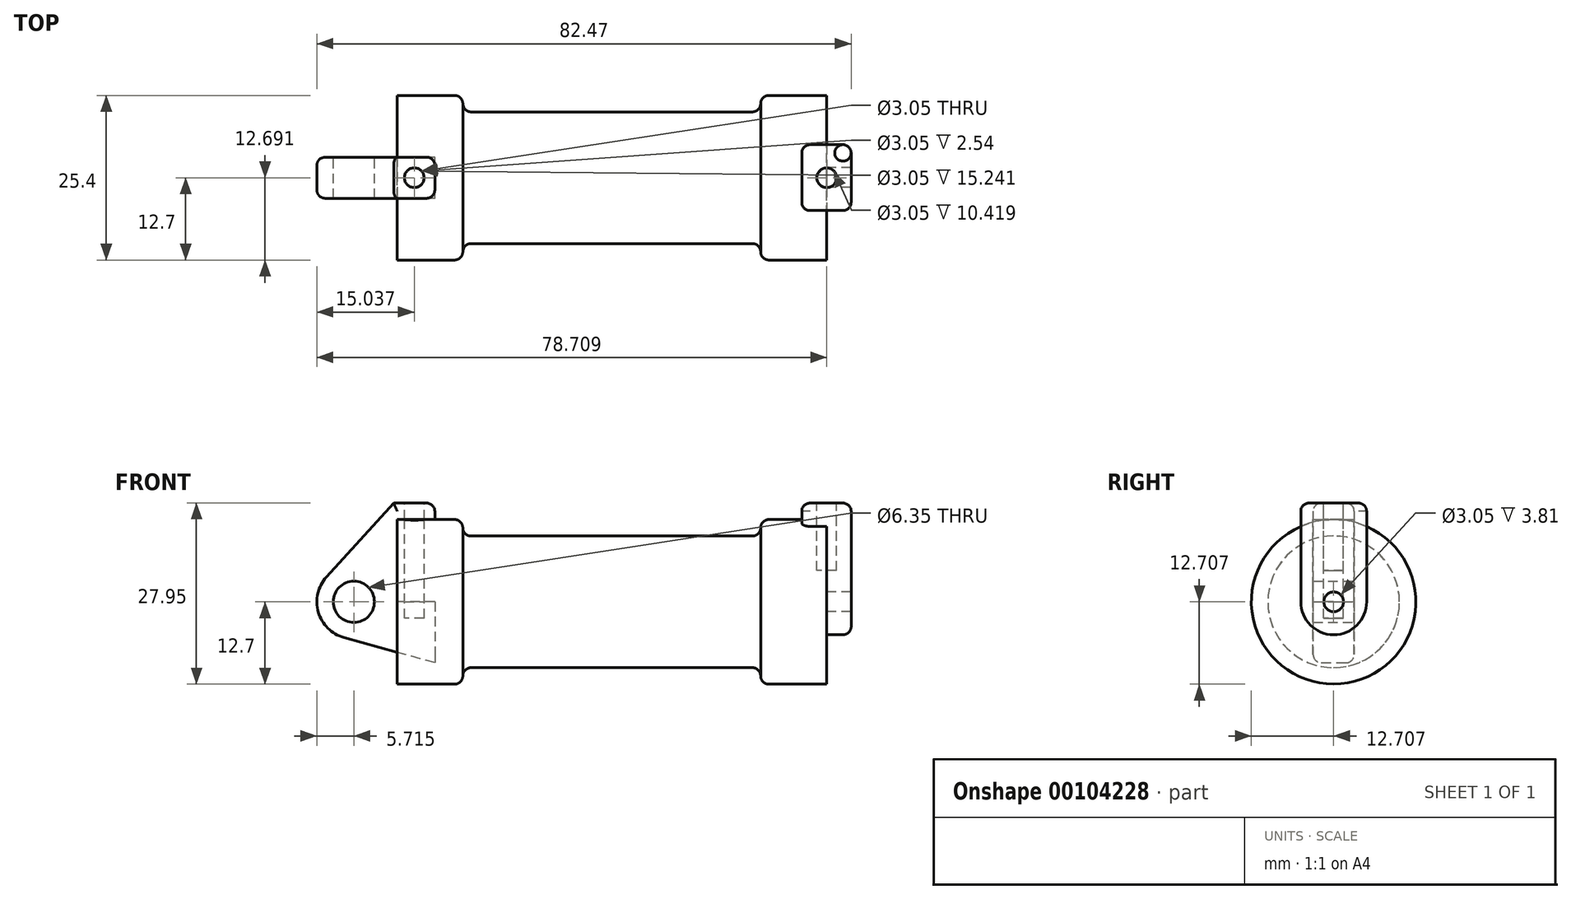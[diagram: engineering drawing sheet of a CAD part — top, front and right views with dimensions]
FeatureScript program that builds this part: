
annotation { "Feature Type Name" : "Feature", "Feature Type Description" : "" }
export const myFeature = defineFeature(function(context is Context, id is Id, definition is map)
    precondition{}
    {
        {
            var Q0;
            Q0=qCreatedBy(makeId("Front.planeOp"),FACE);
            var sketch = newSketch(context, id + "F0", { "sketchPlane" : qUnion([Q0])});
            skLineSegment(sketch, "E0", {"start": v(0, 0) * mm, "end": v(0, 12.7) * mm});
            skLineSegment(sketch, "E1", {"start": v(0, 12.7) * mm, "end": v(10.16, 12.7) * mm});
            skLineSegment(sketch, "E2", {"start": v(10.16, 12.7) * mm, "end": v(10.16, 10.16) * mm});
            skLineSegment(sketch, "E3", {"start": v(10.16, 10.16) * mm, "end": v(56.13, 10.16) * mm});
            skLineSegment(sketch, "E4", {"start": v(56.13, 10.16) * mm, "end": v(56.13, 12.7) * mm});
            skLineSegment(sketch, "E5", {"start": v(56.13, 12.7) * mm, "end": v(66.3, 12.7) * mm});
            skLineSegment(sketch, "E6", {"start": v(66.3, 12.7) * mm, "end": v(66.3, 0) * mm});
            skLineSegment(sketch, "E7", {"start": v(66.3, 0) * mm, "end": v(0, 0) * mm});
            skLineSegment(sketch, "E8", {"start": v(5.84, 15.24) * mm, "end": v(-0.5, 15.24) * mm});
            skLineSegment(sketch, "E9", {"start": v(-0.5, 15.24) * mm, "end": v(-10.88, 3.85) * mm});
            skLineSegment(sketch, "E10", {"start": v(0, 0) * mm, "end": v(-6.65, 0) * mm});
            skCircle(sketch, "E11", {"center": v(-6.65, 0) * mm, "radius": 5.72 * mm});
            skCircle(sketch, "E12", {"center": v(-6.65, 0) * mm, "radius": 3.18 * mm});
            skLineSegment(sketch, "E13", {"start": v(5.84, 15.24) * mm, "end": v(5.84, -9.4) * mm});
            skLineSegment(sketch, "E14", {"start": v(5.84, -9.4) * mm, "end": v(-8.18, -5.5) * mm});
            skSolve(sketch);
        }
        {
            var Q0;
            {var subQ0=sQuery(id+"F0.wireOp",EDGE,"E0");Q0=makeQuery(id+"F0.imprint","IMPRINT",FACE,{"disambiguationData":[TD([[makeQuery(id+"F0.imprint","IMPRINT",EDGE,{"derivedFrom":subQ0}),-1.0]])]});}
            var Q1;
            {var subQ0=sQuery(id+"F0.wireOp",EDGE,"E2");Q1=makeQuery(id+"F0.imprint","IMPRINT",FACE,{"disambiguationData":[TD([[makeQuery(id+"F0.imprint","IMPRINT",EDGE,{"derivedFrom":subQ0}),-1.0]])]});}
            var Q2;
            Q2=sQuery(id+"F0.wireOp",EDGE,"E7");
            revolve(context, id + "F1", {"entities" : qUnion([Q0, Q1]), "axis" : qUnion([Q2]), "revolveType" : RevolveType.FULL});
        }
        {
            var Q0;
            {var subQ4=sQuery(id+"F0.wireOp",EDGE,"E12");Q0=makeQuery(id+"F0.imprint","IMPRINT",FACE,{"disambiguationData":[TD([[makeQuery(id+"F0.imprint","IMPRINT",EDGE,{"derivedFrom":subQ4}),-1.0]])]});}
            var Q1;
            {var subQ3=sQuery(id+"F0.wireOp",EDGE,"E0");Q1=makeQuery(id+"F0.imprint","IMPRINT",FACE,{"disambiguationData":[TD([[makeQuery(id+"F0.imprint","IMPRINT",EDGE,{"derivedFrom":subQ3}),1.0]])]});}
            var Q2;
            {var subQ0=sQuery(id+"F0.wireOp",EDGE,"E14");Q2=makeQuery(id+"F0.imprint","IMPRINT",FACE,{"disambiguationData":[TD([[makeQuery(id+"F0.imprint","IMPRINT",EDGE,{"derivedFrom":subQ0}),-1.0]])]});}
            extrude(context, id + "F2", {"entities" : qUnion([Q0, Q1, Q2]), "endBound" : BoundingType.SYMMETRIC, "depth" : 6.35 * mm});
        }
        {
            var Q0;
            Q0=makeQuery(id+"F1.opRevolve","SWEPT_FACE",FACE,{"disambiguationData":[OSD([sQuery(id+"F0.wireOp",EDGE,"E6")])]});
            var sketch = newSketch(context, id + "F3", { "sketchPlane" : qUnion([Q0])});
            skPoint(sketch, "E15", {"position": v(0, 0) * mm});
            skCircle(sketch, "E16", {"center": v(0, 0) * mm, "radius": 1.52 * mm});
            skCircle(sketch, "E17", {"center": v(0, 0) * mm, "radius": 5.08 * mm});
            skLineSegment(sketch, "E18", {"start": v(-5.07, 0) * mm, "end": v(-5.07, 15.25) * mm});
            skLineSegment(sketch, "E19", {"start": v(-5.07, 15.25) * mm, "end": v(5.1, 15.25) * mm});
            skLineSegment(sketch, "E20", {"start": v(5.1, 15.25) * mm, "end": v(5.09, 0) * mm});
            skSolve(sketch);
        }
        {
            var Q0;
            Q0 = qSketchRegion(id + "F3", true);
            extrude(context, id + "F4", {"entities" : qUnion([Q0]), "operationType" : NewBodyOperationType.ADD, "endBound" : BoundingType.SYMMETRIC, "depth" : 7.62 * mm});
        }
        {
            var Q0;
            Q0=makeQuery(id+"F2.opExtrude","SWEPT_FACE",FACE,{"disambiguationData":[OSD([sQuery(id+"F0.wireOp",EDGE,"E8")])]});
            var sketch = newSketch(context, id + "F5", { "sketchPlane" : qUnion([Q0])});
            skCircle(sketch, "E21", {"center": v(2.67, 0) * mm, "radius": 1.52 * mm});
            skCircle(sketch, "E22", {"center": v(66.34, 0) * mm, "radius": 1.52 * mm});
            skSolve(sketch);
        }
        {
            var Q0;
            Q0=makeQuery(id+"F5.imprint","IMPRINT",FACE,{"disambiguationData":[TD([[makeQuery(id+"F5.imprint","IMPRINT",EDGE,{"derivedFrom":sQuery(id+"F5.wireOp",EDGE,"E21")}),1.0]])]});
            extrude(context, id + "F6", {"entities" : qUnion([Q0]), "operationType" : NewBodyOperationType.REMOVE, "oppositeDirection" : true, "depth" : 17.78 * mm});
        }
        {
            var Q0;
            Q0 = qSketchRegion(id + "F5", true);
            extrude(context, id + "F7", {"entities" : qUnion([Q0]), "operationType" : NewBodyOperationType.REMOVE, "oppositeDirection" : true, "depth" : 10.4 * mm});
        }
        {
            var Q0;
            Q0=makeQuery(id+"F2.opExtrude","CAP_EDGE",EDGE,{"disambiguationData":[OSD([sQuery(id+"F0.wireOp",EDGE,"E8")])],"isStart":true});
            var Q1;
            {var subQ0=sQuery(id+"F0.wireOp",EDGE,"E13");Q1=makeQuery(id+"F2.opExtrude","CAP_EDGE",EDGE,{"disambiguationData":[OSD([subQ0]),TDD([makeQuery(id+"F0.imprint","IMPRINT",EDGE,{"disambiguationData":[TD([[makeQuery(id+"F0.imprint","INTERSECT",VERTEX,{"derivedFrom":[sQuery(id+"F0.wireOp",EDGE,"E8"),subQ0]}),-1.0]])],"derivedFrom":subQ0})])],"isStart":true});}
            var Q2;
            {var subQ0=sQuery(id+"F0.wireOp",EDGE,"E13");Q2=makeQuery(id+"F2.opExtrude","CAP_EDGE",EDGE,{"disambiguationData":[OSD([subQ0]),TDD([makeQuery(id+"F0.imprint","IMPRINT",EDGE,{"disambiguationData":[TD([[makeQuery(id+"F0.imprint","INTERSECT",VERTEX,{"derivedFrom":[sQuery(id+"F0.wireOp",EDGE,"E8"),subQ0]}),-1.0]])],"derivedFrom":subQ0})])],"isStart":false});}
            var Q3;
            Q3=makeQuery(id+"F2.opExtrude","CAP_EDGE",EDGE,{"disambiguationData":[OSD([sQuery(id+"F0.wireOp",EDGE,"E8")])],"isStart":false});
            var Q4;
            Q4=makeQuery(id+"F2.opExtrude","CAP_EDGE",EDGE,{"disambiguationData":[OSD([sQuery(id+"F0.wireOp",EDGE,"E9")])],"isStart":true});
            var Q5;
            Q5=makeQuery(id+"F2.opExtrude","CAP_EDGE",EDGE,{"disambiguationData":[OSD([sQuery(id+"F0.wireOp",EDGE,"E9")])],"isStart":false});
            var Q6;
            Q6=makeQuery(id+"F1.opRevolve","SWEPT_EDGE",EDGE,{"disambiguationData":[OSD([sQuery(id+"F0.wireOp",EDGE,"E1"),sQuery(id+"F0.wireOp",EDGE,"E2")])]});
            var Q7;
            Q7=makeQuery(id+"F1.opRevolve","SWEPT_FACE",FACE,{"disambiguationData":[OSD([sQuery(id+"F0.wireOp",EDGE,"E2")])]});
            var Q8;
            Q8=makeQuery(id+"F1.opRevolve","SWEPT_EDGE",EDGE,{"disambiguationData":[OSD([sQuery(id+"F0.wireOp",EDGE,"E4"),sQuery(id+"F0.wireOp",EDGE,"E5")])]});
            var Q9;
            Q9=makeQuery(id+"F1.opRevolve","SWEPT_EDGE",EDGE,{"disambiguationData":[OSD([sQuery(id+"F0.wireOp",EDGE,"E3"),sQuery(id+"F0.wireOp",EDGE,"E4")])]});
            var Q10;
            Q10=makeQuery(id+"F4.opExtrude","CAP_EDGE",EDGE,{"disambiguationData":[OSD([sQuery(id+"F3.wireOp",EDGE,"E20")])],"isStart":true});
            var Q11;
            Q11=makeQuery(id+"F4.opExtrude","SWEPT_EDGE",EDGE,{"disambiguationData":[OSD([sQuery(id+"F3.wireOp",EDGE,"E19"),sQuery(id+"F3.wireOp",EDGE,"E20")])]});
            var Q12;
            Q12=makeQuery(id+"F4.opExtrude","CAP_EDGE",EDGE,{"disambiguationData":[OSD([sQuery(id+"F3.wireOp",EDGE,"E20")])],"isStart":false});
            var Q13;
            Q13=makeQuery(id+"F4.opExtrude","SWEPT_EDGE",EDGE,{"disambiguationData":[OSD([sQuery(id+"F3.wireOp",EDGE,"E18"),sQuery(id+"F3.wireOp",EDGE,"E19")])]});
            var Q14;
            Q14=makeQuery(id+"F4.opExtrude","CAP_EDGE",EDGE,{"disambiguationData":[OSD([sQuery(id+"F3.wireOp",EDGE,"E18")])],"isStart":true});
            var Q15;
            Q15=makeQuery(id+"F4.opExtrude","CAP_EDGE",EDGE,{"disambiguationData":[OSD([sQuery(id+"F3.wireOp",EDGE,"E19")])],"isStart":false});
            var Q16;
            Q16=makeQuery(id+"F2.opExtrude","SWEPT_EDGE",EDGE,{"disambiguationData":[OSD([sQuery(id+"F0.wireOp",EDGE,"E8"),sQuery(id+"F0.wireOp",EDGE,"E13")])]});
            var Q17;
            Q17=makeQuery(id+"F4.opExtrude","CAP_EDGE",EDGE,{"disambiguationData":[OSD([sQuery(id+"F3.wireOp",EDGE,"E19")])],"isStart":true});
            fillet(context, id + "F8", {"entities" : qUnion([Q0, Q1, Q2, Q3, Q4, Q5, Q6, Q7, Q8, Q9, Q10, Q11, Q12, Q13, Q14, Q15, Q16, Q17]), "radius" : 1.27 * mm, "tangentPropagation" : true, "allowEdgeOverflow" : false});
        }
    });
